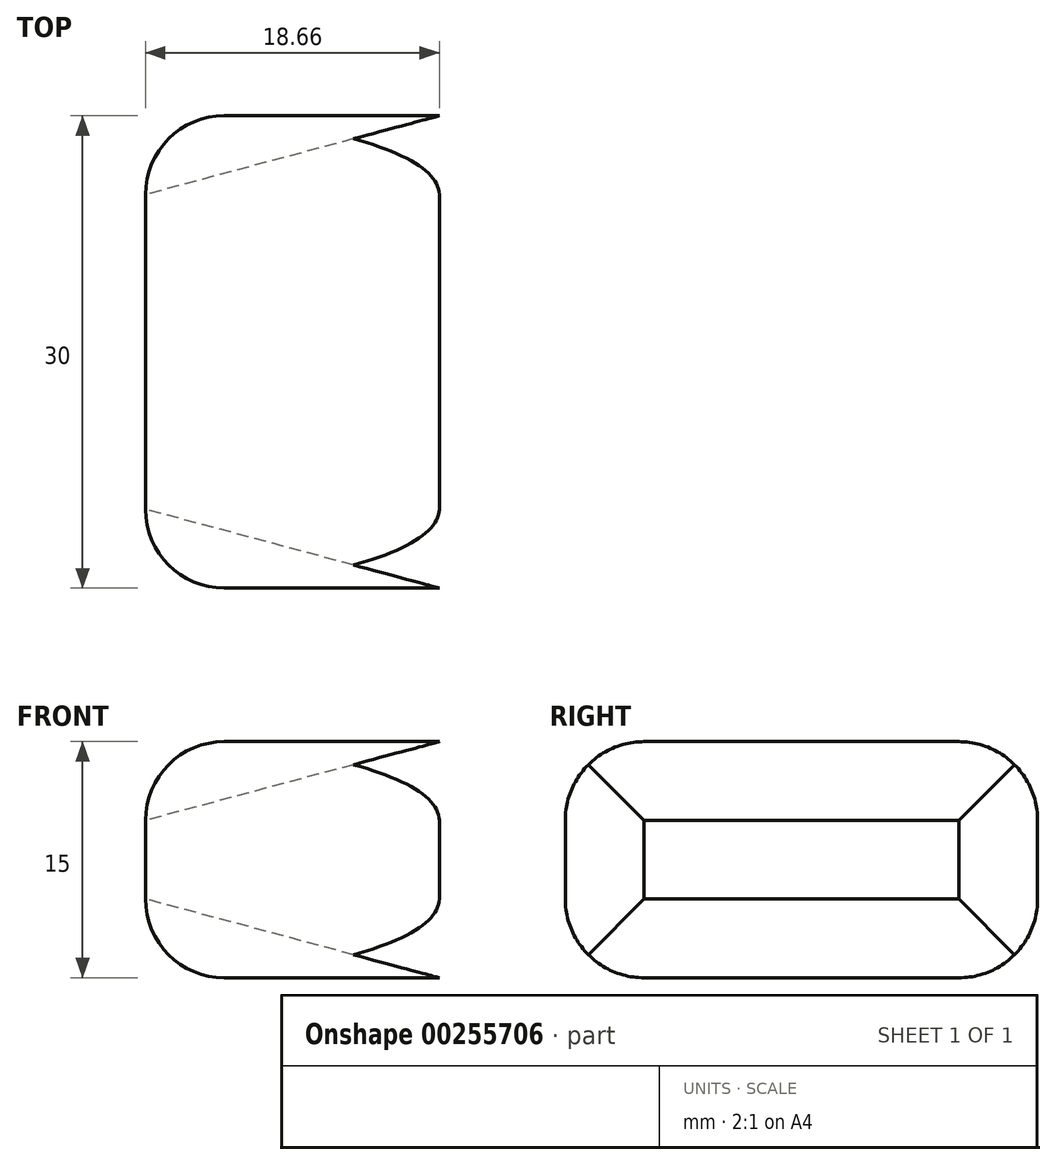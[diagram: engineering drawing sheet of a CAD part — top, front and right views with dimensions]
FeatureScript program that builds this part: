
annotation { "Feature Type Name" : "Feature", "Feature Type Description" : "" }
export const myFeature = defineFeature(function(context is Context, id is Id, definition is map)
    precondition{}
    {
        {
            var Q0;
            Q0=qCreatedBy(makeId("Front.planeOp"),FACE);
            var sketch = newSketch(context, id + "F0", { "sketchPlane" : qUnion([Q0])});
            skLineSegment(sketch, "E0.bottom", {"start": v(-33.19, -1.62) * mm, "end": v(16.81, -1.62) * mm});
            skLineSegment(sketch, "E0.top", {"start": v(-33.19, -16.62) * mm, "end": v(16.81, -16.62) * mm});
            skLineSegment(sketch, "E0.left", {"start": v(-33.19, -1.62) * mm, "end": v(-33.19, -16.62) * mm});
            skLineSegment(sketch, "E0.right", {"start": v(16.81, -1.62) * mm, "end": v(16.81, -16.62) * mm});
            skSolve(sketch);
        }
        {
            var Q0;
            Q0=makeQuery(id+"F0.imprint","IMPRINT",FACE,{"disambiguationData":[TD([[makeQuery(id+"F0.imprint","IMPRINT",EDGE,{"derivedFrom":sQuery(id+"F0.wireOp",EDGE,"E0.bottom")}),-1.0]])]});
            var Q1;
            Q1=sQuery(id+"F0.wireOp",EDGE,"E0.right");
            extrude(context, id + "F1", {"entities" : qUnion([Q0]), "surfaceEntities" : qUnion([Q1]), "depth" : 30 * mm});
        }
        {
            var Q0;
            Q0=makeQuery(id+"F1.opExtrude","SWEPT_FACE",FACE,{"disambiguationData":[OSD([sQuery(id+"F0.wireOp",EDGE,"E0.right")])]});
            var Q1;
            Q1=makeQuery(id+"F1.opExtrude","CAP_FACE",FACE,{"disambiguationData":[OSD([sQuery(id+"F0.wireOp",EDGE,"E0.bottom"),sQuery(id+"F0.wireOp",EDGE,"E0.top"),sQuery(id+"F0.wireOp",EDGE,"E0.left"),sQuery(id+"F0.wireOp",EDGE,"E0.right")])],"isStart":false});
            var Q2;
            Q2=makeQuery(id+"F1.opExtrude","CAP_EDGE",EDGE,{"disambiguationData":[OSD([sQuery(id+"F0.wireOp",EDGE,"E0.right")])],"isStart":true});
            fillet(context, id + "F2", {"entities" : qUnion([Q0, Q1, Q2]), "radius" : 5 * mm, "tangentPropagation" : true, "allowEdgeOverflow" : false});
        }
        {
            var Q0;
            {var subQ0=sQuery(id+"F0.wireOp",EDGE,"E0.right");Q0=makeQuery(id+"F2.opFillet","BLEND_EDGE",EDGE,{"blendedFrom":[makeQuery(id+"F1.opExtrude","CAP_EDGE",EDGE,{"disambiguationData":[OSD([subQ0])],"isStart":true}),makeQuery(id+"F1.opExtrude","CAP_FACE",FACE,{"disambiguationData":[OSD([sQuery(id+"F0.wireOp",EDGE,"E0.bottom"),sQuery(id+"F0.wireOp",EDGE,"E0.top"),sQuery(id+"F0.wireOp",EDGE,"E0.left"),subQ0])],"isStart":true})],"blendedInto":[makeQuery(id+"F1.opExtrude","CAP_FACE",FACE,{"disambiguationData":[OSD([sQuery(id+"F0.wireOp",EDGE,"E0.bottom"),sQuery(id+"F0.wireOp",EDGE,"E0.top"),sQuery(id+"F0.wireOp",EDGE,"E0.left"),subQ0])],"isStart":true})]});}
            var Q1;
            Q1=makeQuery(id+"F1.opExtrude","CAP_FACE",FACE,{"disambiguationData":[OSD([sQuery(id+"F0.wireOp",EDGE,"E0.bottom"),sQuery(id+"F0.wireOp",EDGE,"E0.top"),sQuery(id+"F0.wireOp",EDGE,"E0.left"),sQuery(id+"F0.wireOp",EDGE,"E0.right")])],"isStart":true});
            var Q2;
            {var subQ0=sQuery(id+"F0.wireOp",EDGE,"E0.left");Q2=makeQuery(id+"F2.opFillet","BLEND_EDGE",EDGE,{"blendedFrom":[makeQuery(id+"F1.opExtrude","CAP_EDGE",EDGE,{"disambiguationData":[OSD([subQ0])],"isStart":false}),makeQuery(id+"F1.opExtrude","SWEPT_FACE",FACE,{"disambiguationData":[OSD([subQ0])]})],"blendedInto":[makeQuery(id+"F1.opExtrude","SWEPT_FACE",FACE,{"disambiguationData":[OSD([subQ0])]})]});}
            var Q3;
            Q3=makeQuery(id+"F1.opExtrude","SWEPT_FACE",FACE,{"disambiguationData":[OSD([sQuery(id+"F0.wireOp",EDGE,"E0.left")])]});
            fillet(context, id + "F3", {"entities" : qUnion([Q0, Q1, Q2, Q3]), "radius" : 5 * mm, "tangentPropagation" : true, "allowEdgeOverflow" : false});
        }
        {
            var Q0;
            Q0=makeQuery(id+"F1.opExtrude","SWEPT_FACE",FACE,{"disambiguationData":[OSD([sQuery(id+"F0.wireOp",EDGE,"E0.right")])]});
            extrude(context, id + "F4", {"entities" : qUnion([Q0]), "operationType" : NewBodyOperationType.REMOVE, "oppositeDirection" : true, "depth" : 20 * mm});
        }
        {
            var Q0;
            Q0=makeQuery(id+"F1.opExtrude","SWEPT_FACE",FACE,{"disambiguationData":[OSD([sQuery(id+"F0.wireOp",EDGE,"E0.left")])]});
            extrude(context, id + "F5", {"entities" : qUnion([Q0]), "operationType" : NewBodyOperationType.REMOVE, "oppositeDirection" : true, "depth" : 57.69 * mm, "hasDraft" : true, "draftAngle" : 15 * degree});
        }
    });
